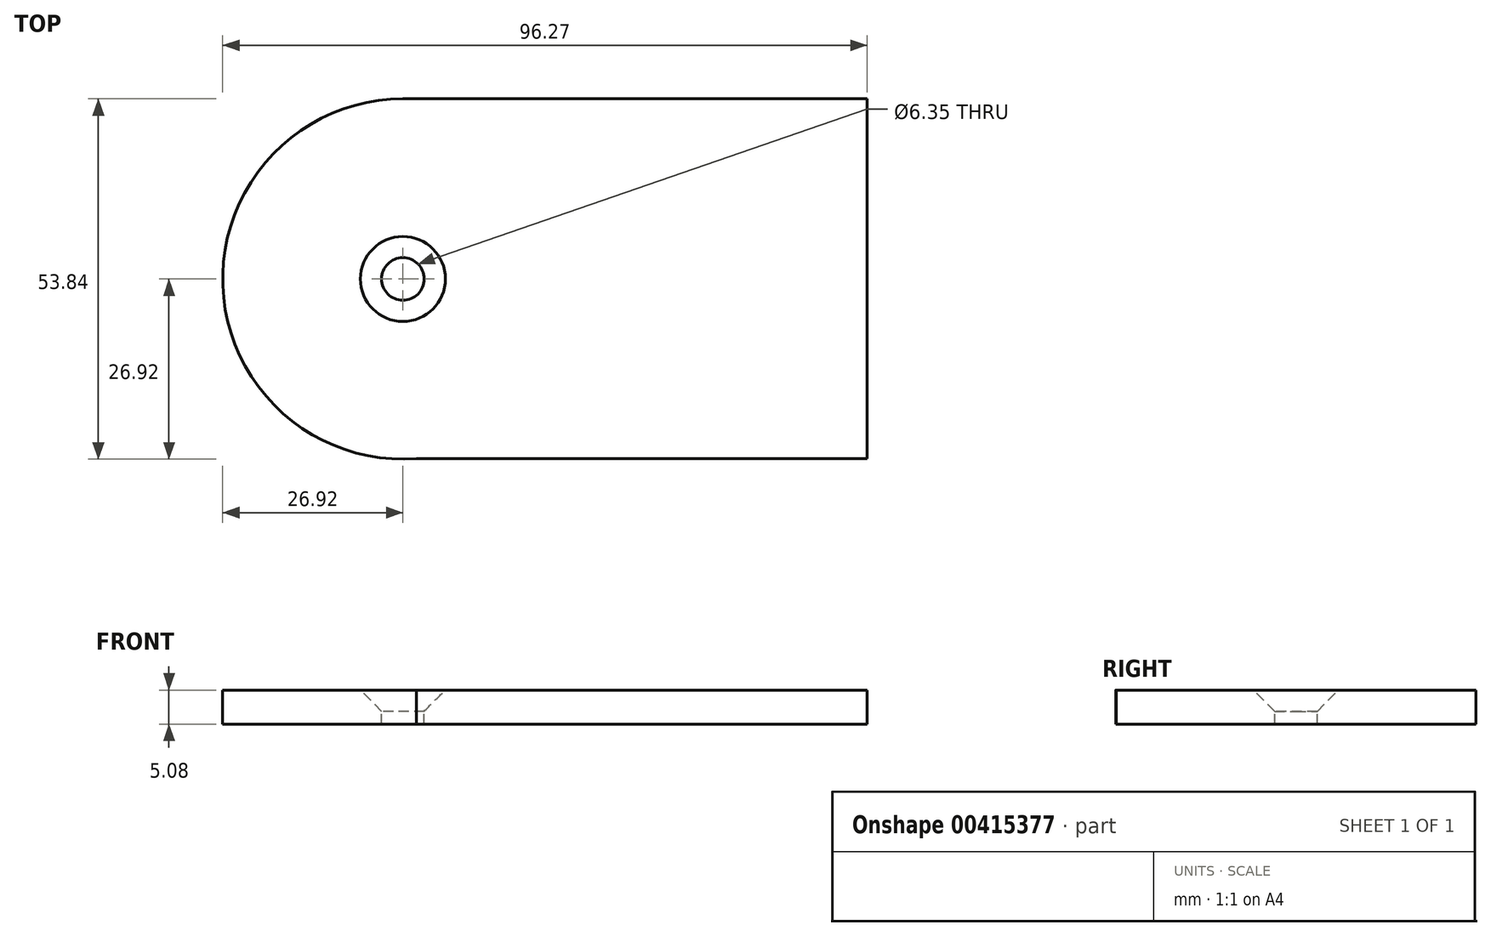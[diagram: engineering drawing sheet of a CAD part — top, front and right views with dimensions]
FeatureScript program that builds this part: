
annotation { "Feature Type Name" : "Feature", "Feature Type Description" : "" }
export const myFeature = defineFeature(function(context is Context, id is Id, definition is map)
    precondition{}
    {
        {
            var Q0;
            Q0=qCreatedBy(makeId("Top.planeOp"),FACE);
            var sketch = newSketch(context, id + "F0", { "sketchPlane" : qUnion([Q0])});
            skCircle(sketch, "E0", {"center": v(0, 0) * mm, "radius": 26.92 * mm});
            skLineSegment(sketch, "E1.bottom", {"start": v(0, 26.92) * mm, "end": v(69.35, 26.92) * mm});
            skLineSegment(sketch, "E1.top", {"start": v(0, -26.84) * mm, "end": v(69.35, -26.84) * mm});
            skLineSegment(sketch, "E1.left", {"start": v(0, 26.92) * mm, "end": v(0, -26.84) * mm});
            skLineSegment(sketch, "E1.right", {"start": v(69.35, 26.92) * mm, "end": v(69.35, -26.84) * mm});
            skSolve(sketch);
        }
        {
            var Q0;
            Q0 = qSketchRegion(id + "F0", true);
            extrude(context, id + "F1", {"entities" : qUnion([Q0]), "depth" : 5.08 * mm});
        }
        {
            var Q0;
            Q0=makeQuery(id+"F1.opExtrude","CAP_FACE",FACE,{"disambiguationData":[OSD([sQuery(id+"F0.wireOp",EDGE,"E0"),sQuery(id+"F0.wireOp",EDGE,"E1.bottom"),sQuery(id+"F0.wireOp",EDGE,"E1.top"),sQuery(id+"F0.wireOp",EDGE,"E1.right")])],"isStart":false});
            var sketch = newSketch(context, id + "F2", { "sketchPlane" : qUnion([Q0])});
            skPoint(sketch, "E2", {"position": v(0, 0) * mm});
            skSolve(sketch);
        }
        {
            var Q0;
            Q0=sQuery(id+"F2.wireOp",VERTEX,"E2");
            var Q1;
            Q1=makeQuery(id+"F1.opExtrude","SWEPT_BODY",BODY,{"disambiguationData":[OSD([sQuery(id+"F0.wireOp",EDGE,"E0"),sQuery(id+"F0.wireOp",EDGE,"E1.bottom"),sQuery(id+"F0.wireOp",EDGE,"E1.top"),sQuery(id+"F0.wireOp",EDGE,"E1.right")])]});
            hole(context, id + "F3", {"style" : HoleStyle.C_SINK, "endStyle" : HoleEndStyle.THROUGH, "holeDiameter" : 6.35 * mm, "cSinkDiameter" : 12.7 * mm, "cSinkAngle" : 90 * degree, "isTappedThrough" : true, "tappedDepth" : 12.7 * mm, "tapClearance" : 3, "locations" : qUnion([Q0]), "scope" : qUnion([Q1])});
        }
    });
